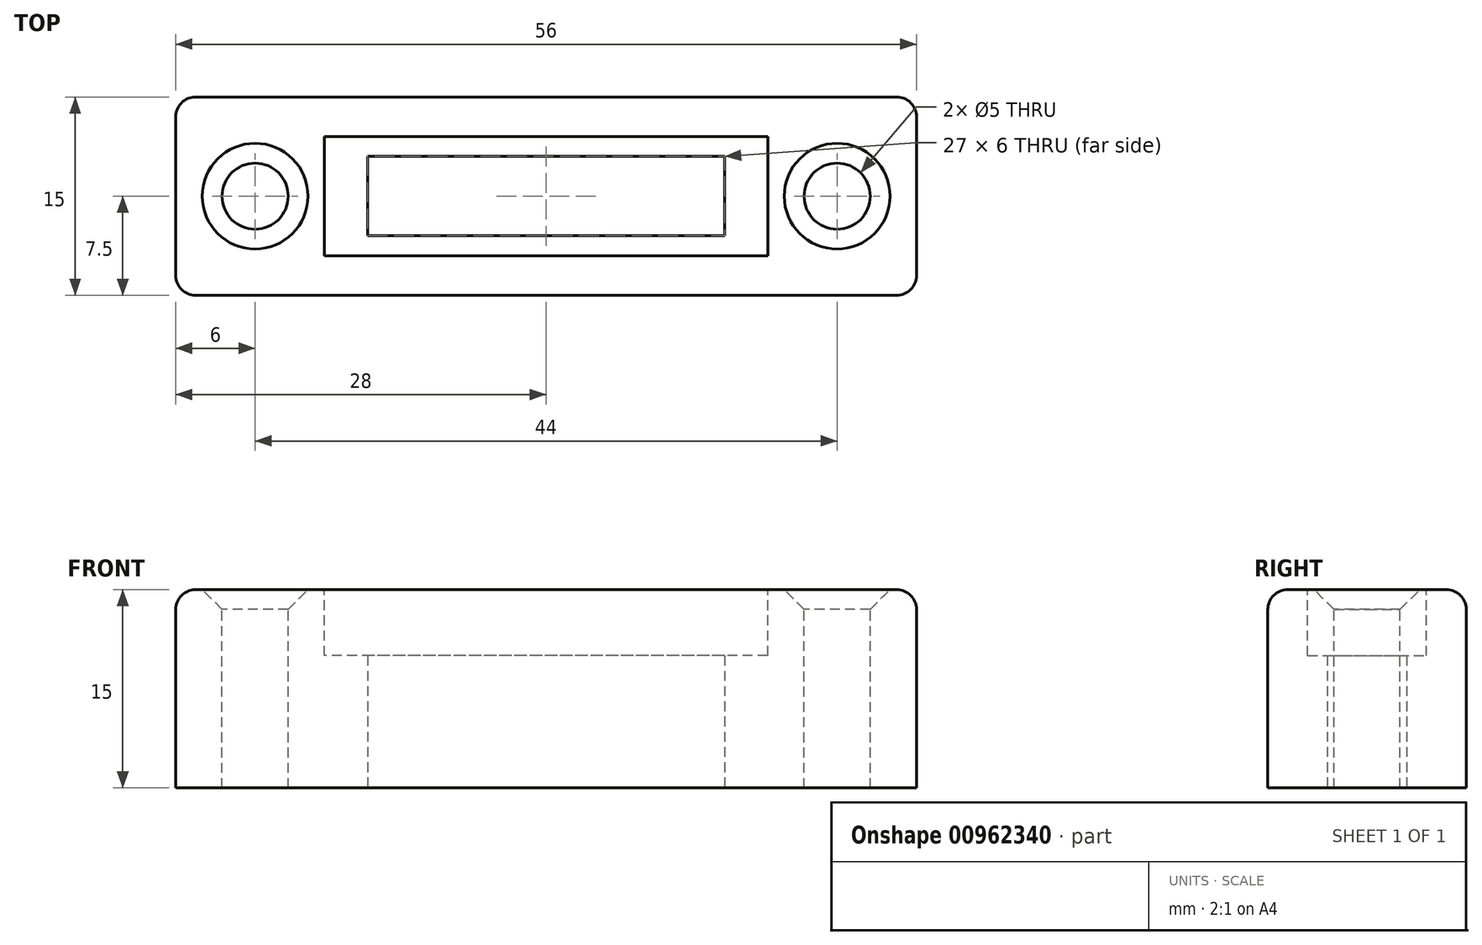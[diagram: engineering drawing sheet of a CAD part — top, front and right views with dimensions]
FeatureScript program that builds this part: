
annotation { "Feature Type Name" : "Feature", "Feature Type Description" : "" }
export const myFeature = defineFeature(function(context is Context, id is Id, definition is map)
    precondition{}
    {
        {
            var Q0;
            Q0=qCreatedBy(makeId("Top.planeOp"),FACE);
            var sketch = newSketch(context, id + "F0", { "sketchPlane" : qUnion([Q0])});
            skLineSegment(sketch, "E0.bottom", {"start": v(26.5, -7.5) * mm, "end": v(-26.5, -7.5) * mm});
            skLineSegment(sketch, "E0.top", {"start": v(26.5, 7.5) * mm, "end": v(-26.5, 7.5) * mm});
            skLineSegment(sketch, "E0.left", {"start": v(28, -6) * mm, "end": v(28, 6) * mm});
            skLineSegment(sketch, "E0.right", {"start": v(-28, -6) * mm, "end": v(-28, 6) * mm});
            skPoint(sketch, "E0.middle", {"position": v(0, 0) * mm});
            skLineSegment(sketch, "E1.bottom", {"start": v(13.5, -3) * mm, "end": v(-13.5, -3) * mm});
            skLineSegment(sketch, "E1.top", {"start": v(13.5, 3) * mm, "end": v(-13.5, 3) * mm});
            skLineSegment(sketch, "E1.left", {"start": v(13.5, -3) * mm, "end": v(13.5, 3) * mm});
            skLineSegment(sketch, "E1.right", {"start": v(-13.5, -3) * mm, "end": v(-13.5, 3) * mm});
            skPoint(sketch, "E2.visualSharp", {"position": v(28, 7.5) * mm});
            skArc(sketch, "E2.filletArc", {"start": v(28, 6) * mm, "mid": v(27.56, 7.06) * mm, "end": v(26.5, 7.5) * mm});
            skPoint(sketch, "E3.visualSharp", {"position": v(28, -7.5) * mm});
            skArc(sketch, "E3.filletArc", {"start": v(26.5, -7.5) * mm, "mid": v(27.56, -7.06) * mm, "end": v(28, -6) * mm});
            skPoint(sketch, "E4.visualSharp", {"position": v(-28, 7.5) * mm});
            skArc(sketch, "E4.filletArc", {"start": v(-26.5, 7.5) * mm, "mid": v(-27.56, 7.06) * mm, "end": v(-28, 6) * mm});
            skPoint(sketch, "E5.visualSharp", {"position": v(-28, -7.5) * mm});
            skArc(sketch, "E5.filletArc", {"start": v(-28, -6) * mm, "mid": v(-27.56, -7.06) * mm, "end": v(-26.5, -7.5) * mm});
            skSolve(sketch);
        }
        {
            var Q0;
            Q0=makeQuery(id+"F0.imprint","IMPRINT",FACE,{"disambiguationData":[TD([[makeQuery(id+"F0.imprint","IMPRINT",EDGE,{"derivedFrom":sQuery(id+"F0.wireOp",EDGE,"E0.bottom")}),-1.0]])]});
            extrude(context, id + "F1", {"entities" : qUnion([Q0]), "depth" : 15 * mm, "offsetDistance" : 25 * mm});
        }
        {
            var Q0;
            Q0=makeQuery(id+"F1.opExtrude","CAP_FACE",FACE,{"disambiguationData":[OSD([sQuery(id+"F0.wireOp",EDGE,"E0.bottom"),sQuery(id+"F0.wireOp",EDGE,"E0.top"),sQuery(id+"F0.wireOp",EDGE,"E0.left"),sQuery(id+"F0.wireOp",EDGE,"E0.right"),sQuery(id+"F0.wireOp",EDGE,"E1.bottom"),sQuery(id+"F0.wireOp",EDGE,"E1.top"),sQuery(id+"F0.wireOp",EDGE,"E1.left"),sQuery(id+"F0.wireOp",EDGE,"E1.right")])],"isStart":false});
            var sketch = newSketch(context, id + "F2", { "sketchPlane" : qUnion([Q0])});
            skPoint(sketch, "E6.0", {"position": v(0, 0) * mm});
            skLineSegment(sketch, "E7.bottom", {"start": v(16.75, -4.5) * mm, "end": v(-16.75, -4.5) * mm});
            skLineSegment(sketch, "E7.top", {"start": v(16.75, 4.5) * mm, "end": v(-16.75, 4.5) * mm});
            skLineSegment(sketch, "E7.left", {"start": v(16.75, -4.5) * mm, "end": v(16.75, 4.5) * mm});
            skLineSegment(sketch, "E7.right", {"start": v(-16.75, -4.5) * mm, "end": v(-16.75, 4.5) * mm});
            skPoint(sketch, "E8", {"position": v(-22, 0) * mm});
            skPoint(sketch, "E9", {"position": v(22, 0) * mm});
            skSolve(sketch);
        }
        {
            var Q0;
            Q0=makeQuery(id+"F1.opExtrude","CAP_FACE",FACE,{"disambiguationData":[OSD([sQuery(id+"F0.wireOp",EDGE,"E0.bottom"),sQuery(id+"F0.wireOp",EDGE,"E0.top"),sQuery(id+"F0.wireOp",EDGE,"E0.left"),sQuery(id+"F0.wireOp",EDGE,"E0.right"),sQuery(id+"F0.wireOp",EDGE,"E1.bottom"),sQuery(id+"F0.wireOp",EDGE,"E1.top"),sQuery(id+"F0.wireOp",EDGE,"E1.left"),sQuery(id+"F0.wireOp",EDGE,"E1.right")])],"isStart":false});
            fillet(context, id + "F3", {"entities" : qUnion([Q0]), "radius" : 1.5 * mm, "tangentPropagation" : true, "allowEdgeOverflow" : false});
        }
        {
            var Q0;
            Q0=makeQuery(id+"F2.imprint","IMPRINT",FACE,{"disambiguationData":[TD([[makeQuery(id+"F2.imprint","IMPRINT",EDGE,{"derivedFrom":sQuery(id+"F2.wireOp",EDGE,"E7.bottom")}),-1.0]])]});
            extrude(context, id + "F4", {"entities" : qUnion([Q0]), "operationType" : NewBodyOperationType.REMOVE, "oppositeDirection" : true, "depth" : 5 * mm, "offsetDistance" : 25 * mm});
        }
        {
            var Q0;
            Q0=sQuery(id+"F2.wireOp",VERTEX,"E8");
            var Q1;
            Q1=sQuery(id+"F2.wireOp",VERTEX,"E9");
            var Q2;
            Q2=makeQuery(id+"F1.opExtrude","SWEPT_BODY",BODY,{"disambiguationData":[OSD([sQuery(id+"F0.wireOp",EDGE,"E0.bottom"),sQuery(id+"F0.wireOp",EDGE,"E0.top"),sQuery(id+"F0.wireOp",EDGE,"E0.left"),sQuery(id+"F0.wireOp",EDGE,"E0.right"),sQuery(id+"F0.wireOp",EDGE,"E1.bottom"),sQuery(id+"F0.wireOp",EDGE,"E1.top"),sQuery(id+"F0.wireOp",EDGE,"E1.left"),sQuery(id+"F0.wireOp",EDGE,"E1.right")])]});
            hole(context, id + "F5", {"style" : HoleStyle.C_SINK, "endStyle" : HoleEndStyle.THROUGH, "holeDiameter" : 5 * mm, "cSinkDiameter" : 8 * mm, "cSinkAngle" : 90 * degree, "majorDiameter" : 5 * mm, "isTappedThrough" : true, "tappedDepth" : 12 * mm, "tapClearance" : 3, "locations" : qUnion([Q0, Q1]), "scope" : qUnion([Q2])});
        }
    });
